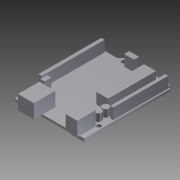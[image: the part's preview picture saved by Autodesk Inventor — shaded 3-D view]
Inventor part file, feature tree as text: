
AUTODESK INVENTOR PART (.ipt)
format: ipt  version: 2011 SP2 (Build 150309200, 309)  size: 207,872 bytes
history: native  units: mm
features: extrude x7, sketch x5
ambient origin geometry x8: Origin, YZ Plane, XZ Plane, XY Plane, X Axis, Y Axis, Z Axis, Center Point
bodies: Solid1 (feature_tree)
feature tree (12):
  extrude  "Extrusion1"  Depth=1.7mm
  extrude  "Extrusion2"  Depth=2.7mm
  extrude  "Extrusion3"  Depth=1.0mm
  sketch  "Sketch4"  dims[d7=3.3mm d8=3.3mm]
  extrude  "Extrusion5"  Depth=3.3mm
  extrude  "Extrusion6"  Depth=3.3mm
  sketch  "Sketch5"  dims[d9=3.3mm d10=3.3mm d11=15.8mm d12=1.0mm d13=1.0mm d14=1.0mm d15=13.8mm d16=12.3mm d17=12.7mm d18=2.503596mm d19=1.8mm d20=1.535884mm d21=53.3mm d22=0.0mm d23=9.1mm d24=9.75mm d25=16.4mm d26=12.2mm d27=8.8mm d28=14.0mm d29=12.4mm d30=1.7mm d31=10.8mm d32=0.0mm d35=1.2mm d36=0.0mm d37=2.4mm d38=0.0mm d39=8.4mm d40=0.0mm d41=5.6mm d42=0.0mm]
  extrude  "Extrusion7"  Depth=15.8mm
  extrude  "Extrusion8"  Depth=1.0mm
  sketch  "Sketch1"  dims[d0=68.9mm d1=1.7mm]
  sketch  "Sketch2"  dims[d2=53.3mm d3=0.0mm d4=2.7mm]
  sketch  "Sketch3"  dims[d5=5.75mm d6=1.0mm]
